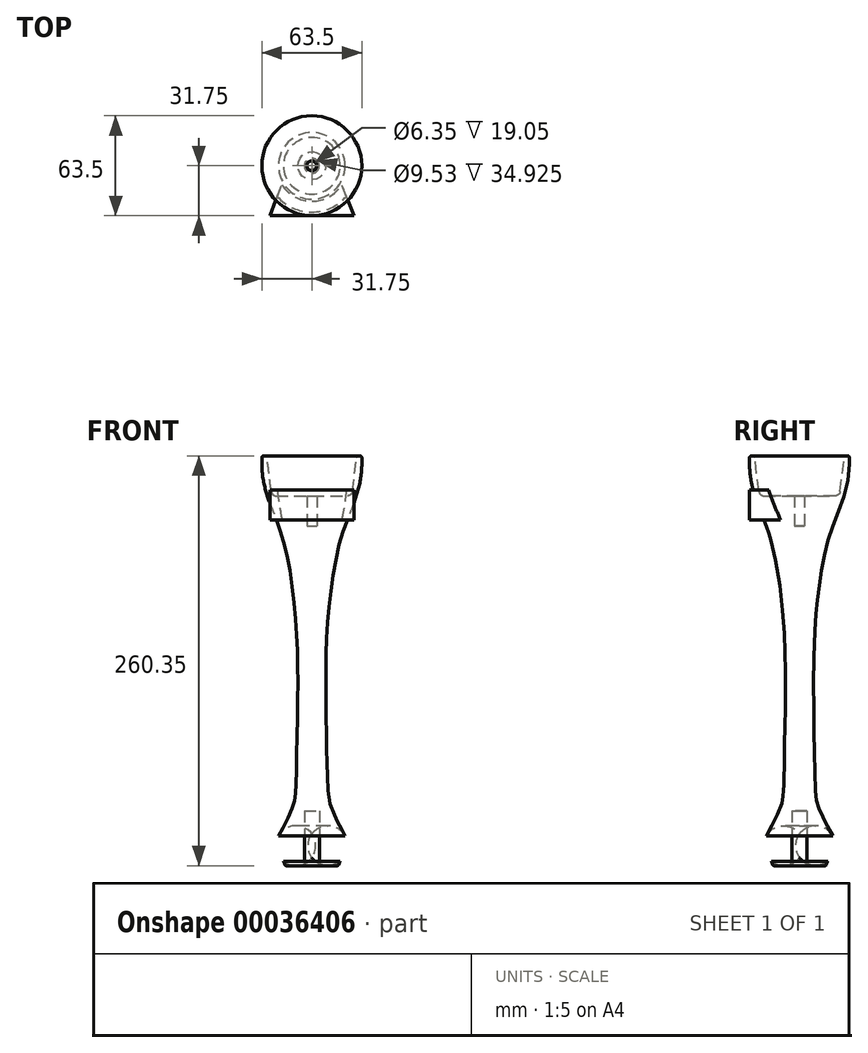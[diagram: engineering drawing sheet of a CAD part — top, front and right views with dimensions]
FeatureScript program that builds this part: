
annotation { "Feature Type Name" : "Feature", "Feature Type Description" : "" }
export const myFeature = defineFeature(function(context is Context, id is Id, definition is map)
    precondition{}
    {
        {
            var Q0;
            Q0=qCreatedBy(makeId("Front.planeOp"),FACE);
            var sketch = newSketch(context, id + "F0", { "sketchPlane" : qUnion([Q0])});
            skLineSegment(sketch, "E0", {"start": v(0, 34.93) * mm, "end": v(0, 215.9) * mm});
            skLineSegment(sketch, "E1", {"start": v(29.7, 260.35) * mm, "end": v(30.48, 260.35) * mm});
            skLineSegment(sketch, "E2", {"start": v(4.76, 0) * mm, "end": v(16.03, 0) * mm});
            skArc(sketch, "E3", {"start": v(21.14, 19.08) * mm, "mid": v(22.63, 10.3) * mm, "end": v(18, 2.7) * mm});
            skLineSegment(sketch, "E4", {"start": v(28.44, 259.23) * mm, "end": v(25.8, 237.74) * mm});
            skLineSegment(sketch, "E5", {"start": v(22.65, 234.95) * mm, "end": v(3.17, 234.95) * mm});
            skLineSegment(sketch, "E6", {"start": v(0, -4.08) * mm, "end": v(0, 315.8) * mm, "construction": true});
            skLineSegment(sketch, "E7", {"start": v(31.75, 259.08) * mm, "end": v(31.75, 255.27) * mm});
            skLineSegment(sketch, "E8", {"start": v(22.86, 48.23) * mm, "end": v(22.86, -30.2) * mm, "construction": true});
            skFitSpline(sketch, "E9", {"points": [v(31.75, 255.27) * mm, v(26.2, 229.15) * mm, v(17.7, 205.24) * mm, v(10.24, 156.74) * mm, v(8.98, 104.41) * mm, v(10.1, 49.84) * mm, v(12, 37.5) * mm, v(21.14, 19.08) * mm], "startDerivative": vector(0, -233.02) * mm, "endDerivative": vector(67.62, -116.36) * mm});
            skPoint(sketch, "E10.visualSharp", {"position": v(25.46, 234.95) * mm});
            skArc(sketch, "E10.filletArc", {"start": v(22.65, 234.95) * mm, "mid": v(24.75, 235.75) * mm, "end": v(25.8, 237.74) * mm});
            skPoint(sketch, "E11.visualSharp", {"position": v(28.57, 260.35) * mm});
            skArc(sketch, "E11.filletArc", {"start": v(29.7, 260.35) * mm, "mid": v(28.86, 260.03) * mm, "end": v(28.44, 259.23) * mm});
            skPoint(sketch, "E12.visualSharp", {"position": v(31.75, 260.35) * mm});
            skArc(sketch, "E12.filletArc", {"start": v(31.75, 259.08) * mm, "mid": v(31.38, 259.98) * mm, "end": v(30.48, 260.35) * mm});
            skLineSegment(sketch, "E13", {"start": v(8.89, 190.62) * mm, "end": v(8.89, 38.13) * mm, "construction": true});
            skLineSegment(sketch, "E14", {"start": v(17.55, 2.03) * mm, "end": v(17.26, 0.94) * mm});
            skPoint(sketch, "E15.visualSharp", {"position": v(17, 0) * mm});
            skArc(sketch, "E15.filletArc", {"start": v(16.03, 0) * mm, "mid": v(16.8, 0.26) * mm, "end": v(17.26, 0.94) * mm});
            skPoint(sketch, "E16.visualSharp", {"position": v(17.66, 2.45) * mm});
            skArc(sketch, "E16.filletArc", {"start": v(18, 2.7) * mm, "mid": v(17.72, 2.4) * mm, "end": v(17.55, 2.03) * mm});
            skLineSegment(sketch, "E17", {"start": v(4.76, 0) * mm, "end": v(4.76, 34.93) * mm});
            skLineSegment(sketch, "E18", {"start": v(4.76, 34.93) * mm, "end": v(0, 34.93) * mm});
            skLineSegment(sketch, "E19", {"start": v(3.17, 234.95) * mm, "end": v(3.18, 215.9) * mm});
            skLineSegment(sketch, "E20", {"start": v(3.18, 215.9) * mm, "end": v(0, 215.9) * mm});
            skPoint(sketch, "E21.orphan", {"position": v(0, 234.95) * mm});
            skSolve(sketch);
        }
        {
            var Q0;
            Q0 = qSketchRegion(id + "F0", true);
            var Q1;
            Q1=sQuery(id+"F0.wireOp",EDGE,"E0");
            revolve(context, id + "F1", {"entities" : qUnion([Q0]), "axis" : qUnion([Q1]), "revolveType" : RevolveType.FULL});
        }
        {
            var Q0;
            Q0=qCreatedBy(makeId("Front.planeOp"),FACE);
            cPlane(context, id + "F2", {"entities" : qUnion([Q0]), "cplaneType" : CPlaneType.OFFSET, "offset" : 31.75 * mm, "width" : 152.4 * mm, "height" : 152.4 * mm});
        }
        {
            var Q0;
            Q0=qCreatedBy(id+"F2.planeOp",FACE);
            var sketch = newSketch(context, id + "F3", { "sketchPlane" : qUnion([Q0])});
            skLineSegment(sketch, "E22.bottom", {"start": v(-19.05, 238.76) * mm, "end": v(19.05, 238.76) * mm});
            skLineSegment(sketch, "E22.top", {"start": v(-19.05, 219.71) * mm, "end": v(19.05, 219.71) * mm});
            skLineSegment(sketch, "E22.left", {"start": v(-19.05, 238.76) * mm, "end": v(-19.05, 219.71) * mm});
            skLineSegment(sketch, "E22.right", {"start": v(19.05, 238.76) * mm, "end": v(19.05, 219.71) * mm});
            skLineSegment(sketch, "E23", {"start": v(0, 0) * mm, "end": v(0, 280.47) * mm, "construction": true});
            skPoint(sketch, "E24", {"position": v(0, 238.76) * mm});
            skSolve(sketch);
        }
        {
            var Q0;
            Q0 = qSketchRegion(id + "F3", true);
            var Q1;
            Q1=makeQuery(id+"F1.opRevolve","SWEPT_FACE",FACE,{"disambiguationData":[OSD([sQuery(id+"F0.wireOp",EDGE,"E9")])]});
            var Q2;
            Q2=makeQuery(id+"F1.opRevolve","SWEPT_BODY",BODY,{"disambiguationData":[OSD([sQuery(id+"F0.wireOp",EDGE,"E0"),sQuery(id+"F0.wireOp",EDGE,"E1"),sQuery(id+"F0.wireOp",EDGE,"E2"),sQuery(id+"F0.wireOp",EDGE,"E3"),sQuery(id+"F0.wireOp",EDGE,"E4"),sQuery(id+"F0.wireOp",EDGE,"E5"),sQuery(id+"F0.wireOp",EDGE,"E7"),sQuery(id+"F0.wireOp",EDGE,"E9"),sQuery(id+"F0.wireOp",EDGE,"E10.filletArc"),sQuery(id+"F0.wireOp",EDGE,"E11.filletArc"),sQuery(id+"F0.wireOp",EDGE,"E12.filletArc")])]});
            extrude(context, id + "F4", {"entities" : qUnion([Q0]), "operationType" : NewBodyOperationType.ADD, "endBound" : BoundingType.UP_TO_NEXT, "oppositeDirection" : true, "endBoundEntityFace" : qUnion([Q1]), "endBoundEntityBody" : qUnion([Q2]), "depth" : 25.4 * mm});
        }
        {
            var Q0;
            Q0=makeQuery(id+"F4.opExtrude","SWEPT_FACE",FACE,{"disambiguationData":[OSD([sQuery(id+"F3.wireOp",EDGE,"E22.bottom")])]});
            var sketch = newSketch(context, id + "F5", { "sketchPlane" : qUnion([Q0])});
            skLineSegment(sketch, "E25", {"start": v(19.05, -31.75) * mm, "end": v(26.67, -31.75) * mm});
            skLineSegment(sketch, "E26", {"start": v(26.67, -31.75) * mm, "end": v(19.05, -12) * mm});
            skLineSegment(sketch, "E27", {"start": v(19.05, -12) * mm, "end": v(19.05, -31.75) * mm});
            skLineSegment(sketch, "E28", {"start": v(0, -31.75) * mm, "end": v(0, -7.24) * mm, "construction": true});
            skLineSegment(sketch, "E29.MirrorCS", {"start": v(-26.67, -31.75) * mm, "end": v(-19.05, -12) * mm});
            skLineSegment(sketch, "E30.MirrorCS", {"start": v(-19.05, -31.75) * mm, "end": v(-26.67, -31.75) * mm});
            skLineSegment(sketch, "E31.MirrorCS", {"start": v(-19.05, -12) * mm, "end": v(-19.05, -31.75) * mm});
            skSolve(sketch);
        }
        {
            var Q0;
            Q0 = qSketchRegion(id + "F5", true);
            var Q1;
            Q1=makeQuery(id+"F4.opExtrude","SWEPT_FACE",FACE,{"disambiguationData":[OSD([sQuery(id+"F3.wireOp",EDGE,"E22.top")])]});
            extrude(context, id + "F6", {"entities" : qUnion([Q0]), "operationType" : NewBodyOperationType.ADD, "endBound" : BoundingType.UP_TO_SURFACE, "oppositeDirection" : true, "endBoundEntityFace" : qUnion([Q1]), "depth" : 25.4 * mm});
        }
        {
            var Q0;
            Q0=qCreatedBy(makeId("Front.planeOp"),FACE);
            var sketch = newSketch(context, id + "F7", { "sketchPlane" : qUnion([Q0])});
            skLineSegment(sketch, "E32.0", {"start": v(29, 263.76) * mm, "end": v(25.8, 237.74) * mm});
            skArc(sketch, "E32.1", {"start": v(22.65, 234.95) * mm, "mid": v(24.75, 235.75) * mm, "end": v(25.8, 237.74) * mm});
            skLineSegment(sketch, "E32.2", {"start": v(22.65, 234.95) * mm, "end": v(0, 234.95) * mm});
            skLineSegment(sketch, "E33.0", {"start": v(0, -4.08) * mm, "end": v(0, 315.8) * mm, "construction": true});
            skLineSegment(sketch, "E34", {"start": v(0, 234.95) * mm, "end": v(0, 263.72) * mm});
            skLineSegment(sketch, "E35", {"start": v(0, 263.72) * mm, "end": v(29, 263.76) * mm});
            skSolve(sketch);
        }
        {
            var Q0;
            Q0 = qSketchRegion(id + "F7", true);
            var Q1;
            Q1=sQuery(id+"F7.wireOp",EDGE,"E33.0");
            revolve(context, id + "F8", {"operationType" : NewBodyOperationType.REMOVE, "entities" : qUnion([Q0]), "axis" : qUnion([Q1]), "revolveType" : RevolveType.FULL, "oppositeDirection" : true});
        }
    });
